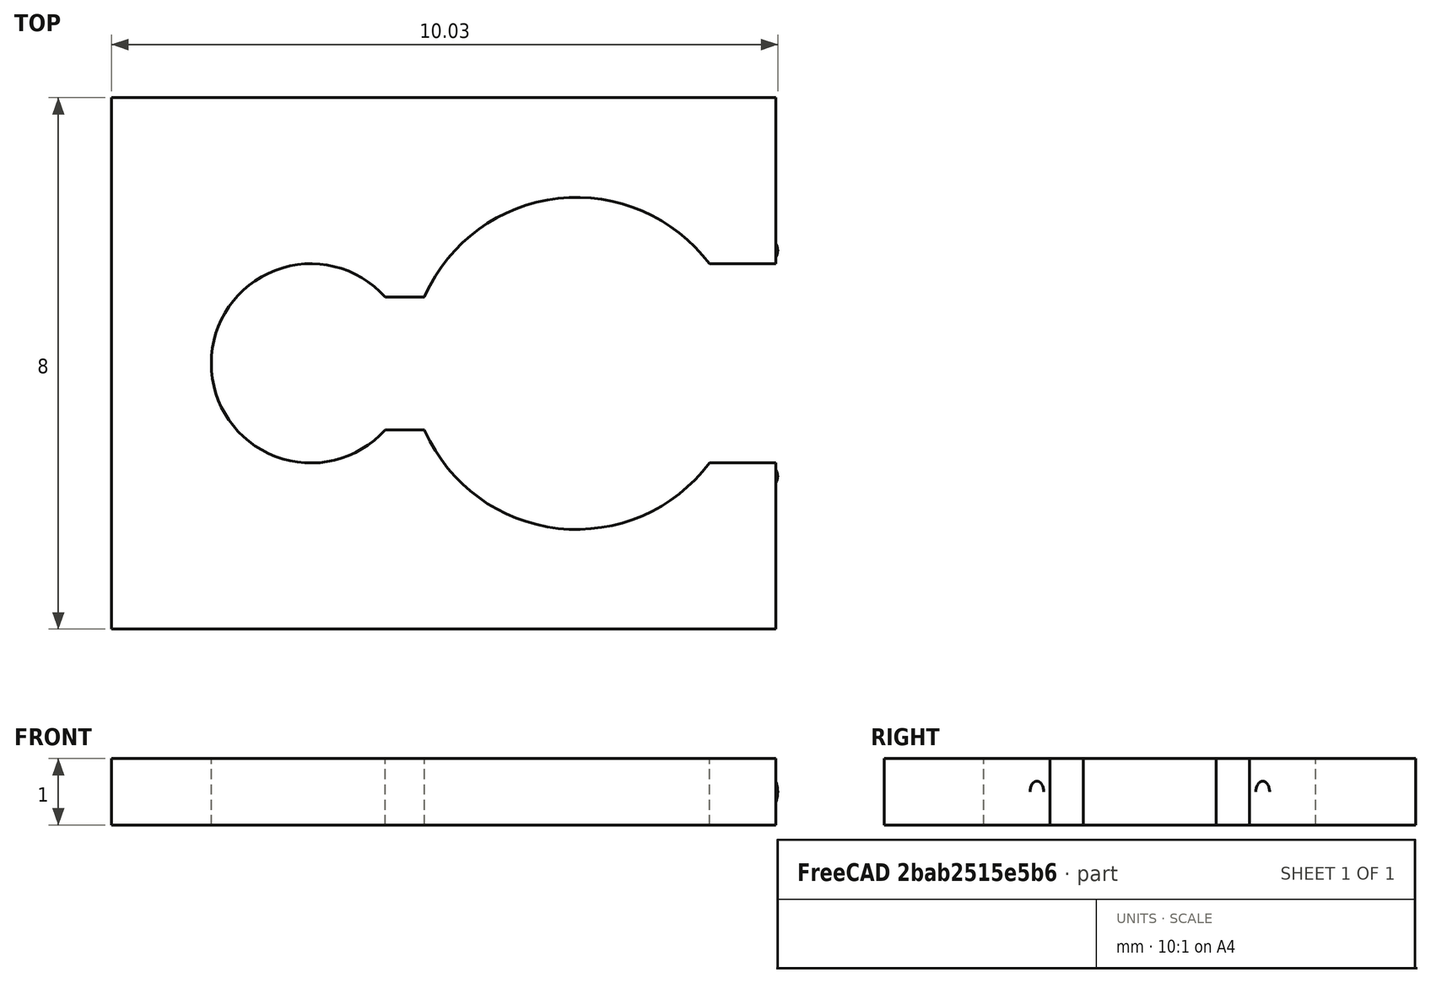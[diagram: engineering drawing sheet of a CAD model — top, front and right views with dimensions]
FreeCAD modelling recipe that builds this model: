
FCSTD DOCUMENT  (FreeCAD 0.16R)
Label: Auriculares Edu V2
License: All rights reserved
LicenseURL: http://en.wikipedia.org/wiki/All_rights_reserved
objects: Part::Cut×8, Part::Box×5, Part::Cylinder×4, Part::Torus×2, Part::MultiFuse×2, PartDesign::Fillet×1
note: 22 computed .brp shape members not serialized (recipe doc carries the construction recipe); baked Part::Feature solids carry a one-line shape summary decoded from their .brp

FEATURE [Part::Torus] Torus  label="Toro"
  Angle1 = -180
  Angle2 = 180
  Angle3 = 360
  Placement = pos=(-1,0,0) rot=(0,0,1;0rad)
  Radius1 = 3
  Radius2 = 0.5
FEATURE [Part::Torus] Torus001  label="Toro001"
  Angle1 = -180
  Angle2 = 180
  Angle3 = 360
  Placement = pos=(-5,0,0) rot=(0,0,1;0rad)
  Radius1 = 2
  Radius2 = 0.5
FEATURE [Part::MultiFuse] Fusion
  Shapes = -> [Torus001,Torus]
FEATURE [Part::Cylinder] Cylinder  label="Cilindro"
  Angle = 360
  Height = 10
  Placement = pos=(-5,0,-4) rot=(0,0,1;0rad)
  Radius = 1.5
FEATURE [Part::Cut] Cut
  Base = -> Fusion
  Tool = -> Cylinder
FEATURE [Part::Cylinder] Cylinder001  label="Cilindro001"
  Angle = 360
  Height = 10
  Placement = pos=(-1,0,-9) rot=(0,0,1;0rad)
  Radius = 2.5
FEATURE [Part::Cut] Cut001
  Base = -> Cut
  Tool = -> Cylinder001
FEATURE [Part::Box] Box  label="Cubo"
  Height = 5
  Length = 3
  Placement = pos=(-4,-0.5,-3) rot=(0,0,1;0rad)
  Width = 1
FEATURE [Part::Cut] Cut002
  Base = -> Cut001
  Tool = -> Box
FEATURE [Part::Box] Box001  label="Cubo001"
  Height = 10
  Length = 4
  Placement = pos=(0,-1.5,-6) rot=(0,0,1;0rad)
  Width = 3
FEATURE [Part::Cut] Cut003
  Base = -> Cut002
  Tool = -> Box001
FEATURE [PartDesign::Fillet] Fillet
  Base = -> Cut003 [Edge34,Edge14,Edge23,Edge25]
  Radius = 0.5
FEATURE [Part::Box] Box002  label="Cubo002"
  Height = 1
  Length = 10
  Placement = pos=(-8,-4,-0.5) rot=(0,0,1;0rad)
  Width = 8
FEATURE [Part::Cylinder] Cylinder002  label="Cilindro002"
  Angle = 360
  Height = 10
  Placement = pos=(-5,0,-1) rot=(0,0,1;0rad)
  Radius = 1.5
FEATURE [Part::MultiFuse] Fusion001
  Shapes = -> [Box002,Fillet]
FEATURE [Part::Cylinder] Cylinder003  label="Cilindro003"
  Angle = 360
  Height = 10
  Placement = pos=(-1,0,-1) rot=(0,0,1;0rad)
  Radius = 2.5
FEATURE [Part::Cut] Cut004
  Base = -> Fusion001
  Tool = -> Cylinder002
FEATURE [Part::Cut] Cut005
  Base = -> Cut004
  Tool = -> Cylinder003
FEATURE [Part::Box] Box003  label="Cubo003"
  Height = 10
  Length = 9
  Placement = pos=(0,-1.5,-3) rot=(0,0,1;0rad)
  Width = 3
FEATURE [Part::Cut] Cut006
  Base = -> Cut005
  Tool = -> Box003
FEATURE [Part::Box] Box004  label="Cubo004"
  Height = 10
  Length = 9
  Placement = pos=(-5,-1,-2) rot=(0,0,1;0rad)
  Width = 2
FEATURE [Part::Cut] Cut007
  Base = -> Cut006
  Tool = -> Box004
